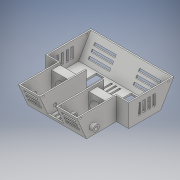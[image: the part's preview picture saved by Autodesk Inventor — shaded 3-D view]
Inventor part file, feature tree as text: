
AUTODESK INVENTOR PART (.ipt)
format: ipt  version: 2018.2 (Build 222227000, 227)  size: 539,136 bytes
history: native  units: mm
features: extrude x29, sketch x29, plane x2
ambient origin geometry x8: Origin, YZ Plane, XZ Plane, XY Plane, X Axis, Y Axis, Z Axis, Center Point
bodies: Solid1 (feature_tree)
feature tree (60):
  extrude  "Extrusion1"  Depth=56.0mm
  extrude  "Extrusion3"  Depth=23.0mm
  extrude  "Extrusion4"  Depth=30.0mm
  extrude  "Extrusion5"  Depth=3.0mm
  extrude  "Extrusion6"  Depth=39.0mm TaperAngle=0.0deg
  extrude  "Extrusion7"  Depth=2.4mm TaperAngle=0.0deg
  extrude  "Extrusion8"  Depth=2.4mm
  extrude  "Extrusion9"  Depth=2.4mm TaperAngle=0.0deg
  extrude  "Extrusion10"  Depth=70.0mm
  extrude  "Extrusion11"  Depth=2.4mm
  extrude  "Extrusion12"  Depth=2.4mm TaperAngle=0.0deg
  extrude  "Extrusion13"  Depth=2.4mm
  extrude  "Extrusion14"  Depth=2.4mm
  extrude  "Extrusion16"  Depth=30.0mm TaperAngle=0.0deg
  extrude  "Extrusion17"  Depth=15.0mm
  extrude  "Extrusion18"  Depth=12.0mm
  extrude  "Extrusion26"  Depth=7.0mm
  extrude  "Extrusion30"  Depth=43.0mm
  extrude  "Extrusion33"  Depth=15.0mm
  extrude  "Extrusion34"  Depth=12.0mm
  extrude  "Extrusion35"  Depth=3.0mm
  extrude  "Extrusion36"  Depth=3.0mm
  extrude  "Extrusion37"  Depth=110.0mm
  plane  "Work Plane1"
  extrude  "Extrusion38"  Depth=5.0mm
  plane  "Work Plane2"
  extrude  "Extrusion39"  Depth=4.0mm TaperAngle=0.0deg
  extrude  "Extrusion40"  Depth=34.0mm TaperAngle=0.0deg
  extrude  "Extrusion41"  Depth=42.0mm
  extrude  "Extrusion42"  Depth=11.0mm TaperAngle=0.0deg
  extrude  "Extrusion43"  Depth=20.0mm TaperAngle=0.0deg
  sketch  "Sketch1"  dims[d0=110.0mm d1=56.0mm]
  sketch  "Sketch3"  dims[d2=23.0mm d3=23.0mm]
  sketch  "Sketch4"  dims[d7=30.0mm d8=30.0mm]
  sketch  "Sketch5"  dims[d9=3.0mm d10=0.0mm d17=60.0mm]
  sketch  "Sketch6"  dims[d18=2.4mm d19=39.0mm d20=0.0mm]
  sketch  "Sketch7"  dims[d21=25.0mm d22=2.4mm d23=0.0mm]
  sketch  "Sketch8"  dims[d24=2.4mm d25=0.0mm d26=2.4mm]
  sketch  "Sketch10"  dims[d27=153.6mm d28=0.0mm d30=2.4mm d31=0.0mm]
  sketch  "Sketch11"  dims[d32=2.4mm d33=0.0mm d37=70.0mm]
  sketch  "Sketch12"  dims[d38=2.4mm d39=2.4mm]
  sketch  "Sketch13"  dims[d40=39.0mm d41=0.0mm d42=2.4mm d43=0.0mm]
  sketch  "Sketch14"  dims[d44=2.4mm d45=0.0mm d46=2.4mm]
  sketch  "Sketch15"  dims[d47=36.0mm d48=0.0mm d49=2.4mm]
  sketch  "Sketch17"  dims[d50=36.0mm d51=0.0mm d52=30.0mm d53=0.0mm]
  sketch  "Sketch18"  dims[d61=43.0mm d62=15.0mm]
  sketch  "Sketch19"  dims[d63=45.0mm d64=12.0mm]
  sketch  "Sketch27"  dims[d65=7.0mm d66=0.0mm d67=5.7mm]
  sketch  "Sketch31"  dims[d68=650.0mm d69=0.0mm d70=43.0mm]
  sketch  "Sketch32"  dims[d71=45.0mm d72=15.0mm]
  sketch  "Sketch33"  dims[d73=12.0mm d74=5.25mm]
  sketch  "Sketch34"  dims[d75=7.0mm d76=0.0mm d170=3.0mm]
  sketch  "Sketch35"  dims[d171=110.0mm d172=3.0mm]
  sketch  "Sketch36"  dims[d173=3.0mm d174=110.0mm]
  sketch  "Sketch37"  dims[d175=13.5mm d176=5.0mm]
  sketch  "Sketch38"  dims[d177=5.0mm d178=4.0mm d179=0.0mm]
  sketch  "Sketch39"  dims[d206=5.0mm d207=34.0mm d208=0.0mm]
  sketch  "Sketch40"  dims[d209=42.0mm d228=26.25mm]
  sketch  "Sketch41"  dims[d229=26.25mm d230=11.0mm d231=0.0mm]
  sketch  "Sketch42"  dims[d232=5.0mm d233=0.0mm d234=20.0mm d235=0.0mm d236=7.0mm d237=55.0mm d238=7.0mm d239=7.0mm d240=55.0mm d241=14.0mm d242=23.0mm d243=0.0mm d244=20.0mm d245=4.0mm d246=4.0mm d247=4.0mm d248=4.0mm d249=156.0mm d250=0.0mm d251=3.0mm d252=3.0mm d253=7.0mm d254=50.0mm d255=0.0mm d256=-25.0mm d257=25.0mm d258=4.0mm d259=4.0mm d260=4.0mm d261=8.0mm d262=25.0mm d263=4.0mm d264=4.0mm d265=8.0mm d266=40.0mm d267=0.0mm d268=25.0mm d269=150.0mm d270=40.0mm d271=4.0mm d272=4.0mm d273=4.0mm d274=40.0mm d275=4.0mm d276=22.0mm d277=22.0mm d278=40.0mm d279=0.0mm d280=10.0mm d281=5.0mm d282=0.0mm d283=10.0mm d284=5.0mm d285=0.0mm d286=23.0mm d287=30.0mm d288=23.0mm d289=7.0mm d290=7.0mm d291=5.0mm d292=0.0mm d293=40.0mm d294=3.0mm d295=3.0mm d296=7.0mm d297=156.0mm d298=0.0mm d299=100.0mm d300=0.0mm]
